# Revit family: Автоматический воздухоотводчик
name_source: partatom
category: Арматура трубопроводов
revit_build: Autodesk Revit 2017 (Build: 20171027_0315(x64)
units: mm (PartAtom-declared; Revit-internal decimal feet)

## family parameters
Всегда вертикально = Да
На основе рабочей плоскости = Нет
Общий = Нет
При загрузке вырезать с полостями = Нет
Размер круглого соединителя = Использовать радиус
Тип детали = Нормальный

## types (1)
- Автоматический воздухоотводчик
    ADSK_Единица измерения = шт
    ADSK_Завод-изготовитель = Meibes
    ADSK_Код изделия = FL89000
    ADSK_Масса = 0
    ADSK_Наименование = Воздухоотводчик автоматический Flexvent с отсечным клапаном
    ADSK_Обозначение = R1/2НР
    DN = 15 мм
    R = 8 мм
    URL = http://www.meibes.ru
    x = 76 мм
    Группа модели = Воздухоотводчик автоматический Flexvent с отсечным клапаном
    Изготовитель = Meibes
    Материал полимера = Фильтр_Черный
    Материал стальной части = Фильтр_Латунь
    Материал фитинга = РВК_Полипропилен PPR
    Разработчик = ООО ПРОРУБИМ
    Разработчик (телефон) = +7(495)649-85-43
    Разработчик модели (URL) = http://prorubim.com
